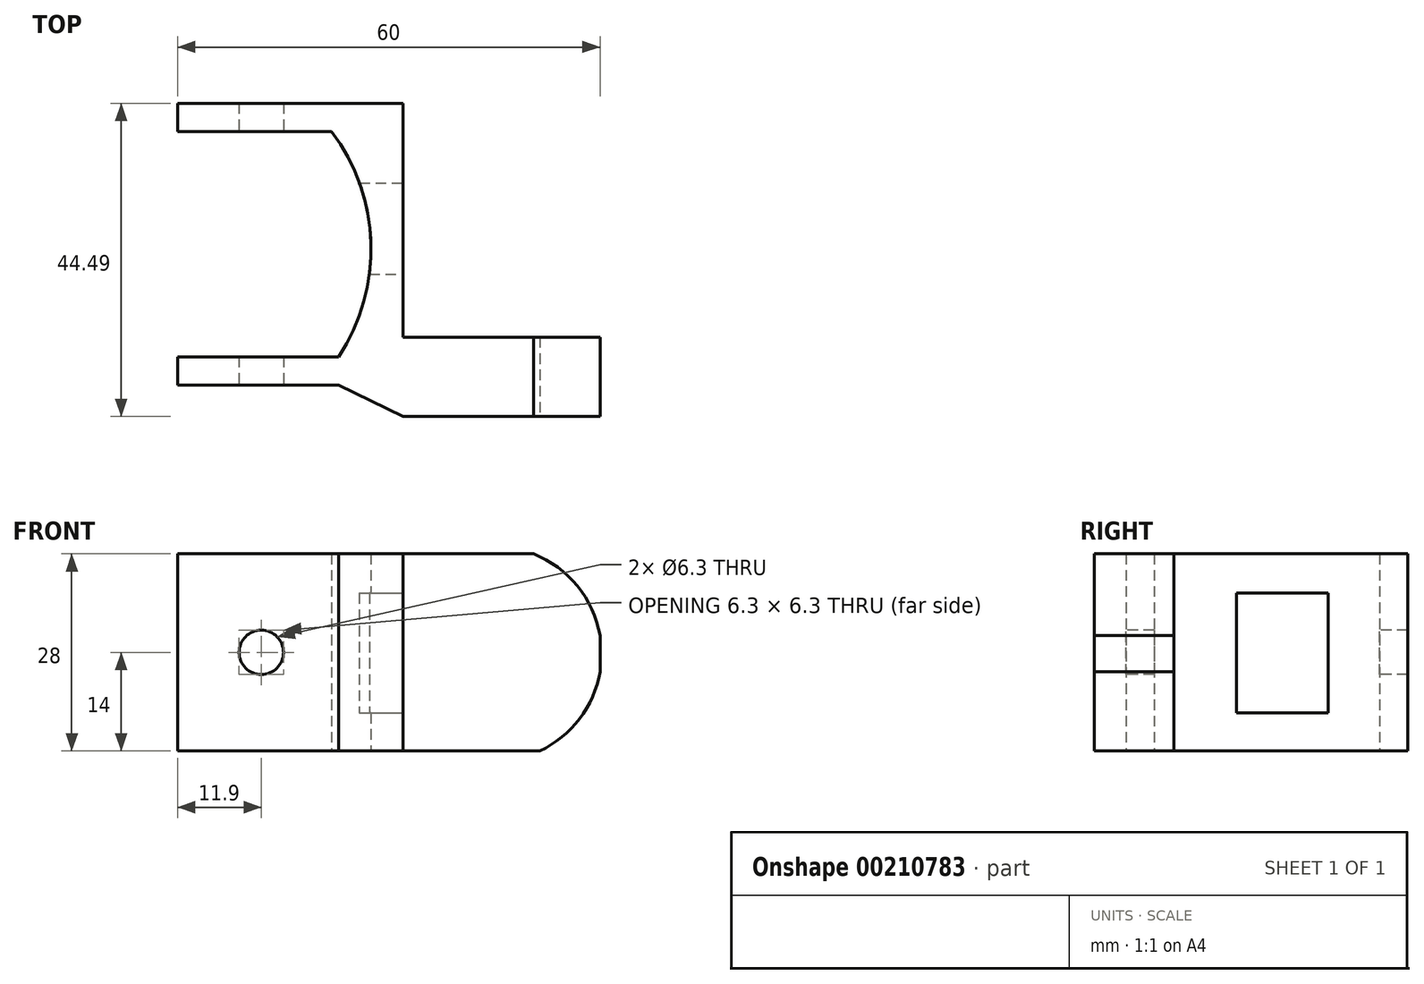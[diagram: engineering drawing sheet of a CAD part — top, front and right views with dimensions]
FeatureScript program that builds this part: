
annotation { "Feature Type Name" : "Feature", "Feature Type Description" : "" }
export const myFeature = defineFeature(function(context is Context, id is Id, definition is map)
    precondition{}
    {
        {
            var Q0;
            Q0=qCreatedBy(makeId("Top.planeOp"),FACE);
            var sketch = newSketch(context, id + "F0", { "sketchPlane" : qUnion([Q0])});
            skLineSegment(sketch, "E0.bottom", {"start": v(-16, 20) * mm, "end": v(16, 20) * mm});
            skLineSegment(sketch, "E0.top", {"start": v(-16, -20) * mm, "end": v(6.86, -20) * mm});
            skLineSegment(sketch, "E0.left", {"start": v(-16, 20) * mm, "end": v(-16, 16) * mm});
            skLineSegment(sketch, "E0.right", {"start": v(16, 20) * mm, "end": v(16, -10) * mm});
            skPoint(sketch, "E0.middle", {"position": v(0, 0) * mm});
            skLineSegment(sketch, "E1.right", {"start": v(44, -20) * mm, "end": v(44, -13.23) * mm});
            skLineSegment(sketch, "E2.bottom", {"start": v(-14, 16) * mm, "end": v(5.89, 16) * mm});
            skLineSegment(sketch, "E2.top", {"start": v(-14, -16) * mm, "end": v(6.86, -16) * mm});
            skLineSegment(sketch, "E3", {"start": v(-14, 16) * mm, "end": v(-16, 16) * mm});
            skLineSegment(sketch, "E4", {"start": v(-14, -16) * mm, "end": v(-16, -16) * mm});
            skLineSegment(sketch, "E5.trimOffspring", {"start": v(-16, -16) * mm, "end": v(-16, -20) * mm});
            skArc(sketch, "E6", {"start": v(6.86, -16) * mm, "mid": v(11.46, 0.16) * mm, "end": v(5.89, 16) * mm});
            skPoint(sketch, "E2.right.start.orphan", {"position": v(14, 16) * mm});
            skPoint(sketch, "E7.orphan", {"position": v(14, -16) * mm});
            skLineSegment(sketch, "E8", {"start": v(6.86, -20) * mm, "end": v(16, -24.49) * mm});
            skLineSegment(sketch, "E9", {"start": v(16, -24.49) * mm, "end": v(44, -24.49) * mm});
            skLineSegment(sketch, "E10", {"start": v(44, -24.49) * mm, "end": v(44, -20) * mm});
            skPoint(sketch, "E11.orphan", {"position": v(16, -20) * mm});
            skLineSegment(sketch, "E12", {"start": v(44, -13.23) * mm, "end": v(16, -13.23) * mm});
            skLineSegment(sketch, "E13", {"start": v(16, -13.23) * mm, "end": v(16, -10) * mm});
            skSolve(sketch);
        }
        {
            var Q0;
            Q0=makeQuery(id+"F0.imprint","IMPRINT",FACE,{"disambiguationData":[TD([[makeQuery(id+"F0.imprint","IMPRINT",EDGE,{"derivedFrom":sQuery(id+"F0.wireOp",EDGE,"E0.bottom")}),-1.0]])]});
            extrude(context, id + "F1", {"entities" : qUnion([Q0]), "depth" : 28 * mm});
        }
        {
            var Q0;
            Q0=makeQuery(id+"F1.opExtrude","SWEPT_FACE",FACE,{"disambiguationData":[OSD([sQuery(id+"F0.wireOp",EDGE,"E0.top"),sQuery(id+"F0.wireOp",EDGE,"E1.bottom")])]});
            var sketch = newSketch(context, id + "F2", { "sketchPlane" : qUnion([Q0])});
            skCircle(sketch, "E14", {"center": v(-4.1, 14) * mm, "radius": 3.15 * mm});
            skPoint(sketch, "E14.centerSnap0", {"position": v(-16, 14) * mm});
            skSolve(sketch);
        }
        {
            var Q0;
            Q0=makeQuery(id+"F2.imprint","IMPRINT",FACE,{"disambiguationData":[TD([[makeQuery(id+"F2.imprint","IMPRINT",EDGE,{"derivedFrom":sQuery(id+"F2.wireOp",EDGE,"E14")}),1.0]])]});
            extrude(context, id + "F3", {"entities" : qUnion([Q0]), "operationType" : NewBodyOperationType.REMOVE, "endBound" : BoundingType.THROUGH_ALL, "oppositeDirection" : true, "depth" : 25 * mm});
        }
        {
            var Q0;
            Q0=makeQuery(id+"F1.opExtrude","SWEPT_FACE",FACE,{"disambiguationData":[OSD([sQuery(id+"F0.wireOp",EDGE,"E0.right")])]});
            var sketch = newSketch(context, id + "F4", { "sketchPlane" : qUnion([Q0])});
            skLineSegment(sketch, "E15.bottom", {"start": v(-4.3, 22.4) * mm, "end": v(8.7, 22.4) * mm});
            skLineSegment(sketch, "E15.top", {"start": v(-4.3, 5.4) * mm, "end": v(8.7, 5.4) * mm});
            skLineSegment(sketch, "E15.left", {"start": v(-4.3, 22.4) * mm, "end": v(-4.3, 5.4) * mm});
            skLineSegment(sketch, "E15.right", {"start": v(8.7, 22.4) * mm, "end": v(8.7, 5.4) * mm});
            skPoint(sketch, "E15.middle", {"position": v(6.5, 14) * mm});
            skPoint(sketch, "E15.middle.positionSnap0", {"position": v(20, 14) * mm});
            skPoint(sketch, "E15.centerSnap0", {"position": v(20, 14) * mm});
            skSolve(sketch);
        }
        {
            var Q0;
            Q0=makeQuery(id+"F4.imprint","IMPRINT",FACE,{"disambiguationData":[TD([[makeQuery(id+"F4.imprint","IMPRINT",EDGE,{"derivedFrom":sQuery(id+"F4.wireOp",EDGE,"E15.bottom")}),-1.0]])]});
            extrude(context, id + "F5", {"entities" : qUnion([Q0]), "operationType" : NewBodyOperationType.REMOVE, "endBound" : BoundingType.THROUGH_ALL, "oppositeDirection" : true, "depth" : 25 * mm});
        }
        {
            var Q0;
            Q0=makeQuery(id+"F1.opExtrude","SWEPT_FACE",FACE,{"disambiguationData":[OSD([sQuery(id+"F0.wireOp",EDGE,"E9")])]});
            var sketch = newSketch(context, id + "F6", { "sketchPlane" : qUnion([Q0])});
            skArc(sketch, "E16", {"start": v(35.43, 0) * mm, "mid": v(44.2, 14.29) * mm, "end": v(34.56, 28) * mm});
            skSolve(sketch);
        }
        {
            var Q0;
            {var subQ0=sQuery(id+"F6.wireOp",EDGE,"E16");var subQ1=sQuery(id+"F0.wireOp",EDGE,"E9");var subQ2=makeQuery(id+"F1.opExtrude","CAP_EDGE",EDGE,{"disambiguationData":[OSD([subQ1])],"isStart":false});var subQ3=makeQuery(id+"F6.imprint","INTERSECT",VERTEX,{"derivedFrom":[subQ2,subQ0]});Q0=makeQuery(id+"F6.imprint","IMPRINT",FACE,{"disambiguationData":[TD([[makeQuery(id+"F6.imprint","IMPRINT",EDGE,{"disambiguationData":[TD([[subQ3,1.0]])],"derivedFrom":subQ0}),-1.0]])]});}
            var Q1;
            {var subQ0=sQuery(id+"F6.wireOp",EDGE,"E16");var subQ1=sQuery(id+"F0.wireOp",EDGE,"E9");var subQ2=makeQuery(id+"F1.opExtrude","CAP_EDGE",EDGE,{"disambiguationData":[OSD([subQ1])],"isStart":true});var subQ3=makeQuery(id+"F6.imprint","INTERSECT",VERTEX,{"derivedFrom":[subQ2,subQ0]});Q1=makeQuery(id+"F6.imprint","IMPRINT",FACE,{"disambiguationData":[TD([[makeQuery(id+"F6.imprint","IMPRINT",EDGE,{"disambiguationData":[TD([[subQ3,-1.0]])],"derivedFrom":subQ0}),-1.0]])]});}
            extrude(context, id + "F7", {"entities" : qUnion([Q0, Q1]), "operationType" : NewBodyOperationType.REMOVE, "endBound" : BoundingType.THROUGH_ALL, "oppositeDirection" : true, "depth" : 25 * mm});
        }
    });
